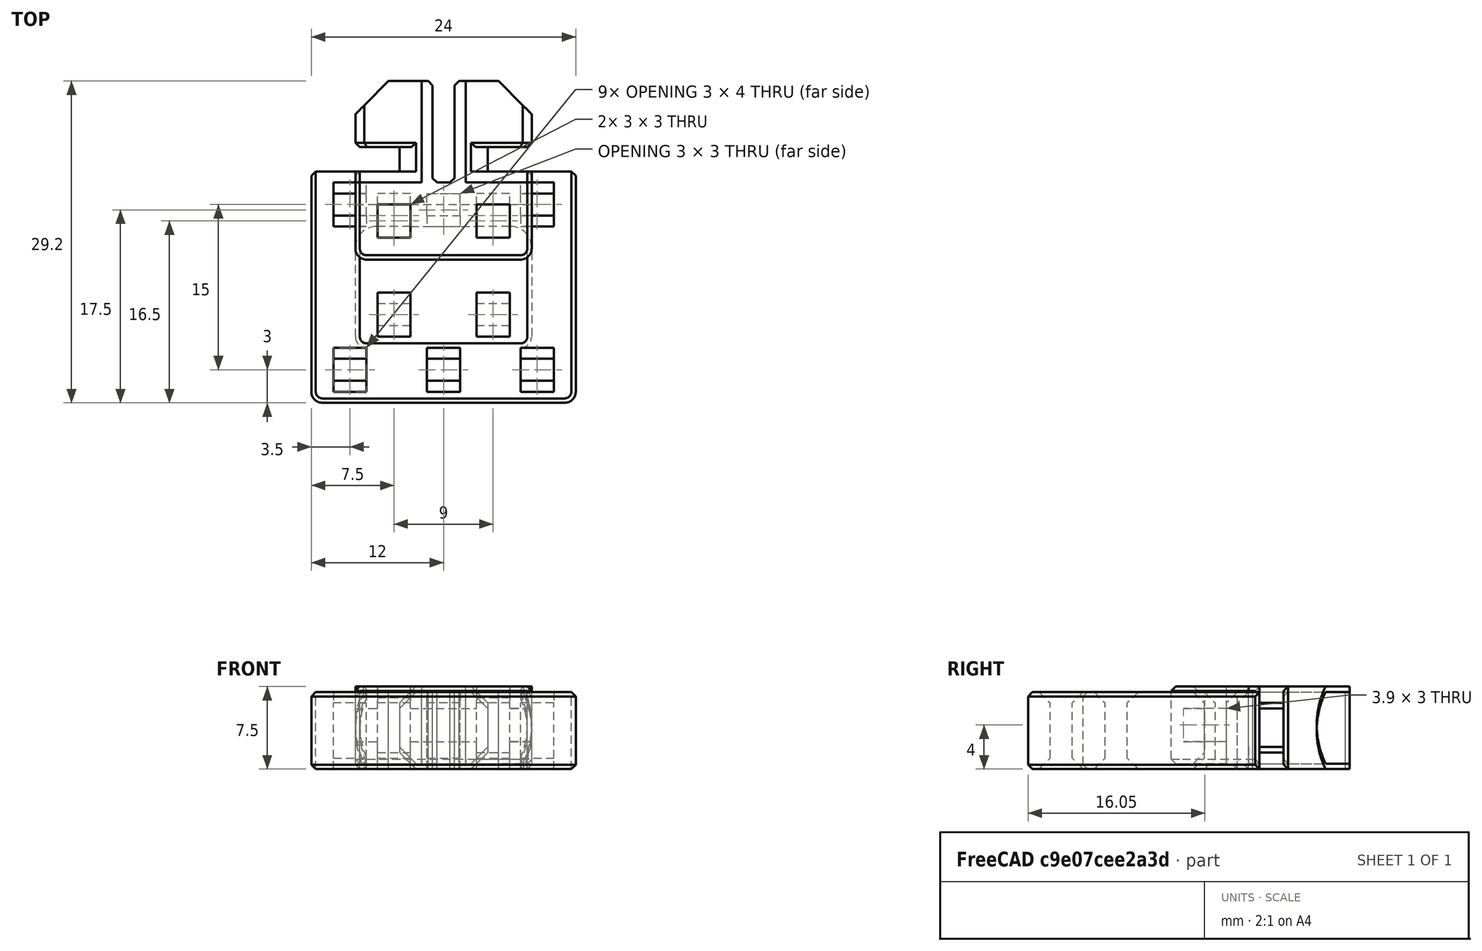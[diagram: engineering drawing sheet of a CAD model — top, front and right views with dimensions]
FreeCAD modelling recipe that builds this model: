
FCSTD DOCUMENT  (FreeCAD 0.19R24291 (Git))
Label: cable-clip
License: Other
LicenseURL: GPL3
objects: Part::Box×30, Part::MultiFuse×10, Part::Chamfer×9, Part::Cut×4, Part::Fillet×4, Part::Feature×3, Part::Refine×3, Part::Cylinder×1, Part::MultiCommon×1
note: 65 computed .brp shape members not serialized (recipe doc carries the construction recipe); baked Part::Feature solids carry a one-line shape summary decoded from their .brp

FEATURE [Part::Box] Box  label="Cube"
  AttacherType = Attacher::AttachEngine3D
  Height = 7
  Length = 2
  Placement = pos=(-4,-1,0.5) rot=(0,0,1;0rad)
  Width = 9
FEATURE [Part::Box] Box001  label="Cube001"
  AttacherType = Attacher::AttachEngine3D
  Height = 7
  Length = 2
  Placement = pos=(2,-1,0.5) rot=(0,0,1;0rad)
  Width = 9
FEATURE [Part::MultiFuse] Fusion
  Shapes = -> [Box,Box001]
FEATURE [Part::Chamfer] Chamfer
  Base = -> Fusion
  Edges = 4 edges r=1.5: [Edge2,Edge4,Edge18,Edge20]
FEATURE [Part::Box] Box002  label="Cube002"
  AttacherType = Attacher::AttachEngine3D
  Height = 7
  Length = 6
  Placement = pos=(-8,-1,0.5) rot=(0,0,1;0rad)
  Width = 1
FEATURE [Part::Box] Box003  label="Cube003"
  AttacherType = Attacher::AttachEngine3D
  Height = 7
  Length = 6
  Placement = pos=(2,2,0.5) rot=(0,0,1;0rad)
  Width = 6
FEATURE [Part::Box] Box004  label="Cube004"
  AttacherType = Attacher::AttachEngine3D
  Height = 7
  Length = 6
  Placement = pos=(-8,2,0.5) rot=(0,0,1;0rad)
  Width = 6
FEATURE [Part::MultiFuse] Fusion001
  Shapes = -> [Box004,Box003]
FEATURE [Part::Chamfer] Chamfer001
  Base = -> Fusion001
  Edges = 2 edges r=3: [Edge3,Edge19]
  Placement = pos=(0,0.2,0) rot=(0,0,1;0rad)
FEATURE [Part::Cylinder] Cylinder
  Angle = 360
  AttacherType = Attacher::AttachEngine3D
  Height = 10
  Placement = pos=(0,1e-15,4) rot=(-1,0,0;1.5708rad)
  Radius = 8
FEATURE [Part::MultiCommon] Common
  Shapes = -> [Cylinder,Chamfer001]
FEATURE [Part::Box] Box005  label="Cube005"
  AttacherType = Attacher::AttachEngine3D
  Height = 7
  Length = 6
  Placement = pos=(2,-1,0.5) rot=(0,0,1;0rad)
  Width = 1
FEATURE [Part::Box] Box006  label="Cube006"
  AttacherType = Attacher::AttachEngine3D
  Height = 7
  Length = 16
  Placement = pos=(-8,-8,0.5) rot=(0,0,1;0rad)
  Width = 7
FEATURE [Part::Chamfer] Chamfer002
  Base = -> Common
  Edges = 8 edges r=0.4: [Edge2,Edge7,Edge8,Edge9,Edge22,Edge23,Edge31,Edge32]
FEATURE [Part::MultiFuse] Fusion002  label="mounter-base"
  Shapes = -> [Chamfer002,Box005,Box002,Chamfer]
FEATURE [Part::Feature] Fusion002001  label="mounter-base001"
  shape: bbox 16 x 9.2 x 7 mm, 60 faces, 2 solids (baked)
FEATURE [Part::Box] Box007  label="Cube007"
  AttacherType = Attacher::AttachEngine3D
  Height = 7
  Length = 3
  Placement = pos=(-6,-5,0.5) rot=(0,0,1;0rad)
  Width = 2
FEATURE [Part::Box] Box008  label="Cube008"
  AttacherType = Attacher::AttachEngine3D
  Height = 7
  Length = 3
  Placement = pos=(3,-5,0.5) rot=(0,0,1;0rad)
  Width = 2
FEATURE [Part::MultiFuse] Fusion002002
  Shapes = -> [Box008,Box007]
FEATURE [Part::Cut] Cut
  Base = -> Box006
  Tool = -> Fusion002002
FEATURE [Part::Chamfer] Chamfer003
  Base = -> Cut
  Edges = 4 edges r=1: [Edge11,Edge15,Edge22,Edge26]
FEATURE [Part::Box] Box010  label="Cube010"
  AttacherType = Attacher::AttachEngine3D
  Height = 3
  Length = 18
  Placement = pos=(-9,-5,2.5) rot=(0,0,1;0rad)
  Width = 2
FEATURE [Part::Cut] Cut001
  Base = -> Chamfer003
  Tool = -> Box010
FEATURE [Part::Fillet] Fillet
  Base = -> Cut001
  Edges = 2 edges r=1: [Edge27,Edge35]
FEATURE [Part::Fillet] Fillet001
  Base = -> Fillet
  Edges = 2 edges r=1.9: [Edge25,Edge37]
FEATURE [Part::MultiFuse] Fusion002003
  Shapes = -> [Fillet001,Fusion002001]
FEATURE [Part::Box] Box011  label="Cube011"
  AttacherType = Attacher::AttachEngine3D
  Height = 7
  Length = 1
  Placement = pos=(-2,-1,0.5) rot=(0,0,1;0rad)
  Width = 9.2
FEATURE [Part::Box] Box012  label="Cube012"
  AttacherType = Attacher::AttachEngine3D
  Height = 7
  Length = 1
  Placement = pos=(1,-1,0.5) rot=(0,0,1;0rad)
  Width = 9.2
FEATURE [Part::MultiFuse] Fusion002004
  Shapes = -> [Box012,Fusion002003,Box011]
FEATURE [Part::Refine] Fusion002004001
  Source = -> Fusion002004
FEATURE [Part::Chamfer] Chamfer004  label="short"
  Base = -> Fusion002004001
  Edges = 16 edges r=0.4: [Edge1,Edge3,Edge7,Edge9,Edge17,Edge18,Edge19,Edge20,Edge21,Edge44,Edge63,Edge66,Edge68,Edge77,Edge166,Edge167]
FEATURE [Part::Feature] Fusion002004002  label="mounter-base002"
  Placement = pos=(0,0,-0.5) rot=(0,0,1;0rad)
  shape: bbox 16 x 9.2 x 7 mm, 60 faces, 2 solids (baked)
FEATURE [Part::Box] Box013  label="Cube013"
  AttacherType = Attacher::AttachEngine3D
  Height = 7
  Length = 16
  Placement = pos=(-8,-16,0) rot=(0,0,1;0rad)
  Width = 15
FEATURE [Part::Box] Box014  label="Cube014"
  AttacherType = Attacher::AttachEngine3D
  Height = 7
  Length = 1
  Placement = pos=(-2,-1,0) rot=(0,0,1;0rad)
  Width = 9.2
FEATURE [Part::Box] Box015  label="Cube015"
  AttacherType = Attacher::AttachEngine3D
  Height = 7
  Length = 1
  Placement = pos=(1,-1,0) rot=(0,0,1;0rad)
  Width = 9.2
FEATURE [Part::Fillet] Fillet002
  Base = -> Box013
  Edges = 2 edges r=1: [Edge1,Edge5]
FEATURE [Part::MultiFuse] Fusion002004003
  Shapes = -> [Fillet002,Box015,Box014,Fusion002004002]
FEATURE [Part::Refine] Fusion002004003001
  Source = -> Fusion002004003
FEATURE [Part::Chamfer] Chamfer005
  Base = -> Fusion002004003001
  Edges = 16 edges r=0.4: [Edge1,Edge3,Edge7,Edge9,Edge17,Edge18,Edge19,Edge20,Edge21,Edge36,Edge55,Edge58,Edge60,Edge69,Edge92,Edge93]
FEATURE [Part::Box] Box016  label="Cube016"
  AttacherType = Attacher::AttachEngine3D
  Height = 10
  Length = 3
  Placement = pos=(-6,-5,0) rot=(0,0,1;0rad)
  Width = 2
FEATURE [Part::Box] Box017  label="Cube017"
  AttacherType = Attacher::AttachEngine3D
  Height = 10
  Length = 3
  Placement = pos=(3,-5,0) rot=(0,0,1;0rad)
  Width = 2
FEATURE [Part::Box] Box018  label="Cube018"
  AttacherType = Attacher::AttachEngine3D
  Height = 10
  Length = 3
  Placement = pos=(3,-14,0) rot=(0,0,1;0rad)
  Width = 2
FEATURE [Part::Box] Box019  label="Cube019"
  AttacherType = Attacher::AttachEngine3D
  Height = 10
  Length = 3
  Placement = pos=(-6,-14,0) rot=(0,0,1;0rad)
  Width = 2
FEATURE [Part::MultiFuse] Fusion002004003002
  Shapes = -> [Box019,Box018,Box017,Box016]
FEATURE [Part::Cut] Cut002
  Base = -> Chamfer005
  Tool = -> Fusion002004003002
FEATURE [Part::Chamfer] Chamfer006  label="long"
  Base = -> Cut002
  Edges = 16 edges r=1: [Edge28,Edge30,Edge32,Edge34,Edge36,Edge38,Edge40,Edge42,Edge68,Edge70,Edge72,Edge74,Edge76,Edge78,Edge80,Edge82]
FEATURE [Part::Box] Box020  label="Cube020"
  AttacherType = Attacher::AttachEngine3D
  Height = 7
  Length = 1
  Placement = pos=(-2,-1,0) rot=(0,0,1;0rad)
  Width = 9.2
FEATURE [Part::Box] Box021  label="Cube021"
  AttacherType = Attacher::AttachEngine3D
  Height = 7
  Length = 1
  Placement = pos=(1,-1,0) rot=(0,0,1;0rad)
  Width = 9.2
FEATURE [Part::Box] Box022  label="Cube022"
  AttacherType = Attacher::AttachEngine3D
  Height = 7
  Length = 24
  Placement = pos=(-12,-21,0) rot=(0,0,1;0rad)
  Width = 20
FEATURE [Part::Feature] Fusion002004003004  label="mounter-base003"
  Placement = pos=(0,0,-0.5) rot=(0,0,1;0rad)
  shape: bbox 16 x 9.2 x 7 mm, 60 faces, 2 solids (baked)
FEATURE [Part::Box] Box023  label="Cube023"
  AttacherType = Attacher::AttachEngine3D
  Height = 7
  Length = 11
  Placement = pos=(-12,-1,0) rot=(0,0,1;0rad)
  Width = 1
FEATURE [Part::Box] Box024  label="Cube024"
  AttacherType = Attacher::AttachEngine3D
  Height = 7
  Length = 11
  Placement = pos=(1,-1,0) rot=(0,0,1;0rad)
  Width = 1
FEATURE [Part::Fillet] Fillet003
  Base = -> Box022
  Edges = 2 edges r=1: [Edge1,Edge5]
FEATURE [Part::MultiFuse] Fusion002004003005
  Shapes = -> [Fillet003,Box024,Box023,Fusion002004003004,Box021,Box020]
FEATURE [Part::Refine] Fusion002004003005001
  Source = -> Fusion002004003005
FEATURE [Part::Box] Box025  label="Cube025"
  AttacherType = Attacher::AttachEngine3D
  Height = 10
  Length = 3
  Placement = pos=(-10,-4,0) rot=(0,0,1;0rad)
  Width = 2
FEATURE [Part::Box] Box026  label="Cube026"
  AttacherType = Attacher::AttachEngine3D
  Height = 10
  Length = 3
  Placement = pos=(7,-4,0) rot=(0,0,1;0rad)
  Width = 2
FEATURE [Part::Box] Box027  label="Cube027"
  AttacherType = Attacher::AttachEngine3D
  Height = 10
  Length = 3
  Placement = pos=(-1.5,-4,0) rot=(0,0,1;0rad)
  Width = 2
FEATURE [Part::Box] Box028  label="Cube028"
  AttacherType = Attacher::AttachEngine3D
  Height = 10
  Length = 3
  Placement = pos=(-1.5,-19,0) rot=(0,0,1;0rad)
  Width = 2
FEATURE [Part::Box] Box029  label="Cube029"
  AttacherType = Attacher::AttachEngine3D
  Height = 10
  Length = 3
  Placement = pos=(7,-19,0) rot=(0,0,1;0rad)
  Width = 2
FEATURE [Part::Box] Box030  label="Cube030"
  AttacherType = Attacher::AttachEngine3D
  Height = 10
  Length = 3
  Placement = pos=(-10,-19,0) rot=(0,0,1;0rad)
  Width = 2
FEATURE [Part::Chamfer] Chamfer007
  Base = -> Fusion002004003005001
  Edges = 16 edges r=0.4: [Edge2,Edge4,Edge6,Edge15,Edge16,Edge17,Edge18,Edge19,Edge51,Edge54,Edge56,Edge86,Edge87,Edge92,Edge93,Edge94]
FEATURE [Part::MultiFuse] Fusion002004003005002
  Shapes = -> [Box030,Box025,Box026,Box027,Box028,Box029]
FEATURE [Part::Cut] Cut003
  Base = -> Chamfer007
  Tool = -> Fusion002004003005002
FEATURE [Part::Chamfer] Chamfer008  label="big"
  Base = -> Cut003
  Edges = 22 edges r=1: [Edge28,Edge30,Edge32,Edge34,Edge38,Edge40,Edge42,Edge44,Edge46,Edge48,Edge50,Edge76,Edge78,Edge80,Edge82,Edge84,Edge86,Edge88,Edge90,Edge92,Edge96,Edge98]
